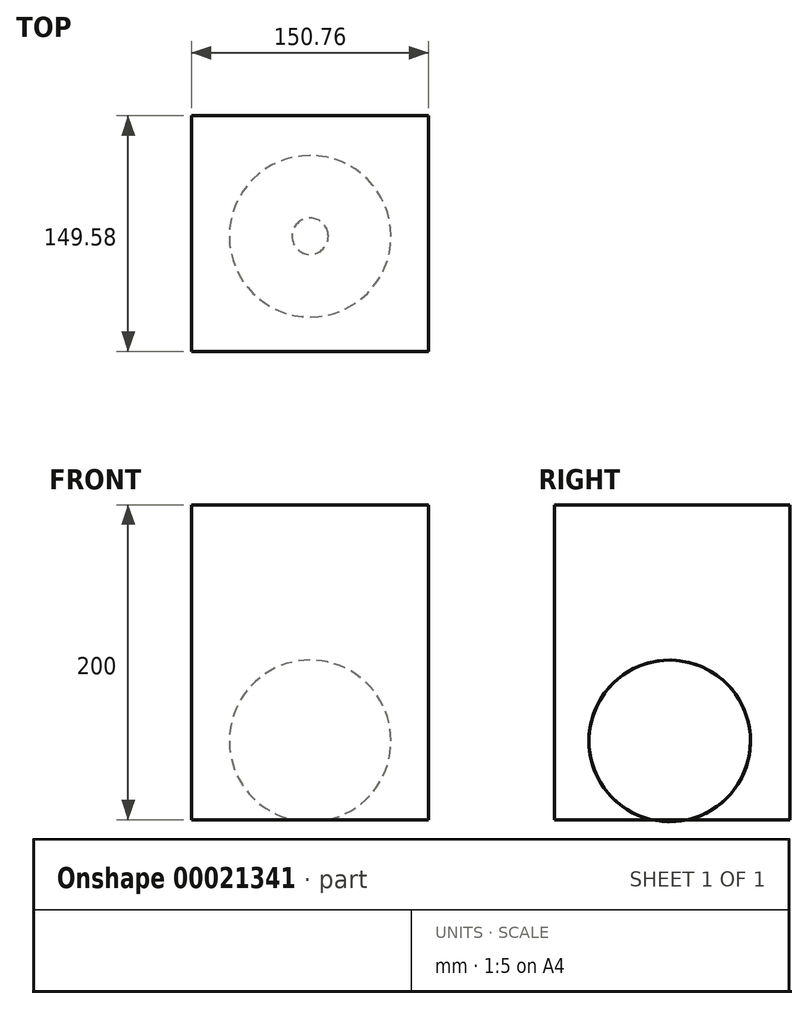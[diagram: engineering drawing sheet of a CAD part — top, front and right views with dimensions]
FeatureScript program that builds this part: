
annotation { "Feature Type Name" : "Feature", "Feature Type Description" : "" }
export const myFeature = defineFeature(function(context is Context, id is Id, definition is map)
    precondition{}
    {
        {
            var Q0;
            Q0=qCreatedBy(makeId("Top.planeOp"),FACE);
            var sketch = newSketch(context, id + "F0", { "sketchPlane" : qUnion([Q0])});
            skArc(sketch, "E0", {"start": v(0, 51.32) * mm, "mid": v(-51.32, 0) * mm, "end": v(0, -51.32) * mm});
            skLineSegment(sketch, "E1", {"start": v(0, -75.84) * mm, "end": v(0, 75.54) * mm});
            skSolve(sketch);
        }
        {
            var Q0;
            Q0 = qSketchRegion(id + "F0", true);
            var Q1;
            Q1=sQuery(id+"F0.wireOp",EDGE,"E1");
            revolve(context, id + "F1", {"entities" : qUnion([Q0]), "axis" : qUnion([Q1]), "revolveType" : RevolveType.FULL});
        }
        {
            var Q0;
            Q0=qCreatedBy(makeId("Top.planeOp"),FACE);
            cPlane(context, id + "F2", {"entities" : qUnion([Q0]), "cplaneType" : CPlaneType.OFFSET, "offset" : 150 * mm, "width" : 150 * mm, "height" : 150 * mm});
        }
        {
            var Q0;
            Q0=qCreatedBy(id+"F2.planeOp",FACE);
            var sketch = newSketch(context, id + "F3", { "sketchPlane" : qUnion([Q0])});
            skLineSegment(sketch, "E2.bottom", {"start": v(-75.5, -73.1) * mm, "end": v(75.27, -73.1) * mm});
            skLineSegment(sketch, "E2.top", {"start": v(-75.5, 76.49) * mm, "end": v(75.27, 76.49) * mm});
            skLineSegment(sketch, "E2.left", {"start": v(-75.5, -73.1) * mm, "end": v(-75.5, 76.49) * mm});
            skLineSegment(sketch, "E2.right", {"start": v(75.27, -73.1) * mm, "end": v(75.27, 76.49) * mm});
            skSolve(sketch);
        }
        {
            var Q0;
            Q0 = qSketchRegion(id + "F3", true);
            extrude(context, id + "F4", {"entities" : qUnion([Q0]), "oppositeDirection" : true, "depth" : 200 * mm});
        }
        {
            var Q0;
            Q0=makeQuery(id+"F1.opRevolve","SWEPT_BODY",BODY,{"disambiguationData":[OSD([sQuery(id+"F0.wireOp",EDGE,"E0"),sQuery(id+"F0.wireOp",EDGE,"E1")])]});
            var Q1;
            Q1=makeQuery(id+"F4.opExtrude","SWEPT_BODY",BODY,{"disambiguationData":[OSD([sQuery(id+"F3.wireOp",EDGE,"E2.bottom"),sQuery(id+"F3.wireOp",EDGE,"E2.top"),sQuery(id+"F3.wireOp",EDGE,"E2.left"),sQuery(id+"F3.wireOp",EDGE,"E2.right")])]});
            booleanBodies(context, id + "F5", {"operationType" : BooleanOperationType.SUBTRACTION, "tools" : qUnion([Q0]), "targets" : qUnion([Q1])});
        }
    });
